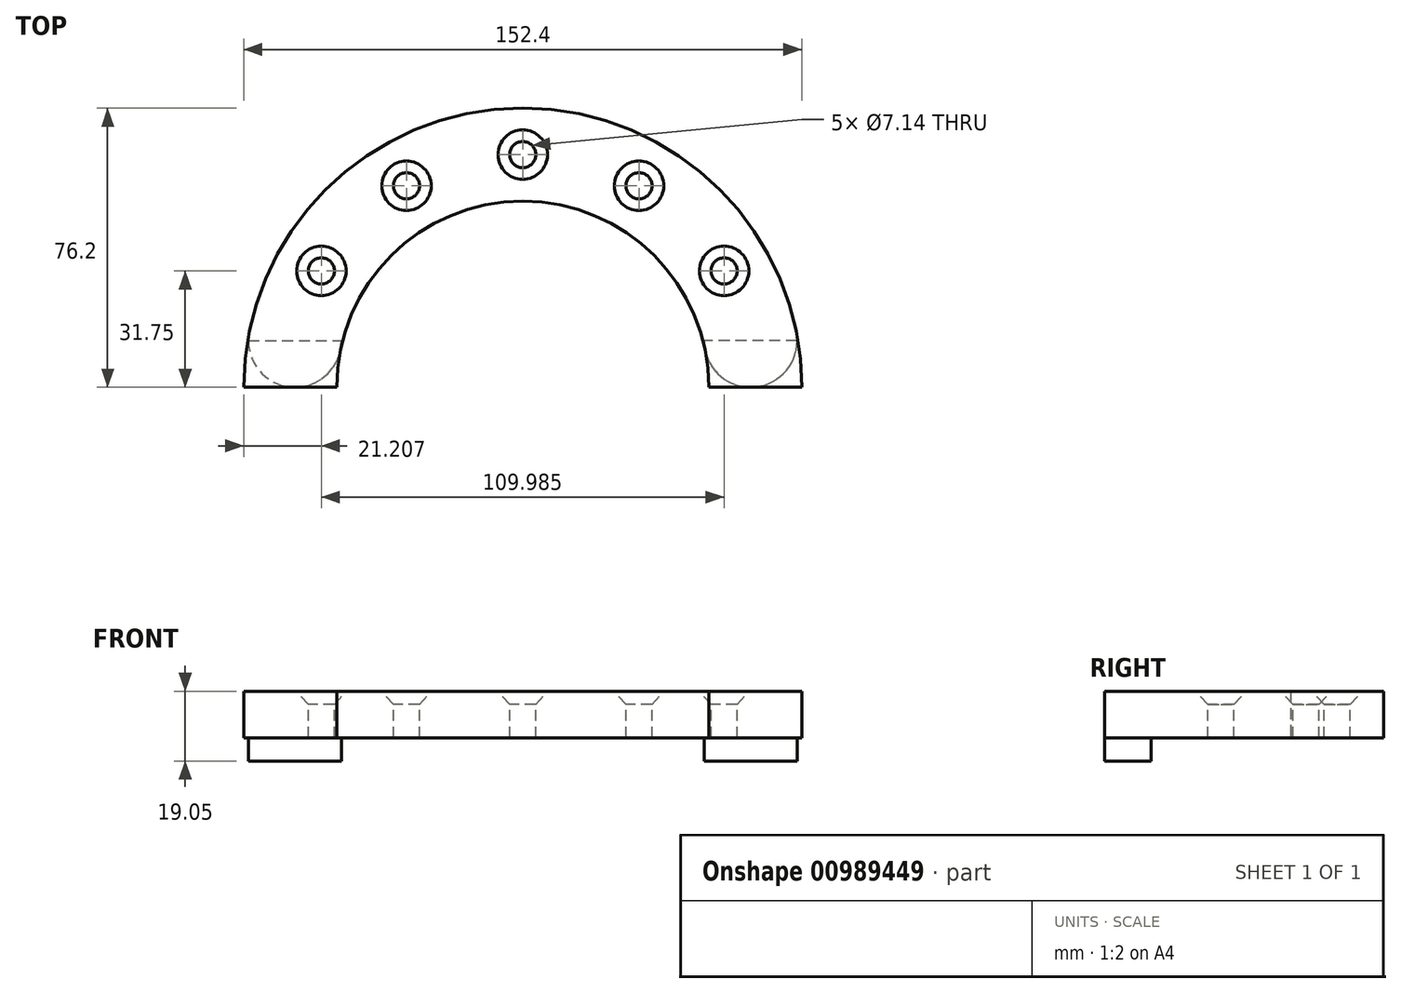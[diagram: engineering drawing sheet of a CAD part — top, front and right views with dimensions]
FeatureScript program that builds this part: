
annotation { "Feature Type Name" : "Feature", "Feature Type Description" : "" }
export const myFeature = defineFeature(function(context is Context, id is Id, definition is map)
    precondition{}
    {
        {
            var Q0;
            Q0=qCreatedBy(makeId("Top.planeOp"),FACE);
            var sketch = newSketch(context, id + "F0", { "sketchPlane" : qUnion([Q0])});
            skArc(sketch, "E0", {"start": v(-50.8, 0) * mm, "mid": v(0, 50.8) * mm, "end": v(50.8, 0) * mm});
            skArc(sketch, "E1", {"start": v(76.2, 0) * mm, "mid": v(0, 76.2) * mm, "end": v(-76.2, 0) * mm});
            skLineSegment(sketch, "E2", {"start": v(-76.2, 0) * mm, "end": v(-50.8, 0) * mm});
            skLineSegment(sketch, "E3", {"start": v(50.8, 0) * mm, "end": v(76.2, 0) * mm});
            skSolve(sketch);
        }
        {
            var Q0;
            Q0 = qSketchRegion(id + "F0", true);
            extrude(context, id + "F1", {"entities" : qUnion([Q0]), "depth" : 12.7 * mm, "offsetDistance" : 25.4 * mm});
        }
        {
            var Q0;
            Q0=makeQuery(id+"F1.opExtrude","CAP_FACE",FACE,{"disambiguationData":[OSD([sQuery(id+"F0.wireOp",EDGE,"E0"),sQuery(id+"F0.wireOp",EDGE,"E1"),sQuery(id+"F0.wireOp",EDGE,"E2"),sQuery(id+"F0.wireOp",EDGE,"E3")])],"isStart":true});
            var sketch = newSketch(context, id + "F2", { "sketchPlane" : qUnion([Q0])});
            skArc(sketch, "E4", {"start": v(-49.52, -12.7) * mm, "mid": v(-62.22, 0) * mm, "end": v(-74.92, -12.7) * mm});
            skLineSegment(sketch, "E5", {"start": v(-74.92, -12.7) * mm, "end": v(-49.52, -12.7) * mm});
            skLineSegment(sketch, "E6", {"start": v(0, 0) * mm, "end": v(0, -90.53) * mm, "construction": true});
            skPoint(sketch, "E6.endSnap0", {"position": v(0, -76.2) * mm});
            skArc(sketch, "E7.MirrorCS", {"start": v(49.52, -12.7) * mm, "mid": v(62.22, 0) * mm, "end": v(74.92, -12.7) * mm});
            skLineSegment(sketch, "E8.MirrorCS", {"start": v(74.92, -12.7) * mm, "end": v(49.52, -12.7) * mm});
            skSolve(sketch);
        }
        {
            var Q0;
            Q0 = qSketchRegion(id + "F2", true);
            extrude(context, id + "F3", {"entities" : qUnion([Q0]), "operationType" : NewBodyOperationType.ADD, "depth" : 6.35 * mm, "offsetDistance" : 25.4 * mm});
        }
        {
            var Q0;
            Q0=makeQuery(id+"F1.opExtrude","CAP_FACE",FACE,{"disambiguationData":[OSD([sQuery(id+"F0.wireOp",EDGE,"E0"),sQuery(id+"F0.wireOp",EDGE,"E1"),sQuery(id+"F0.wireOp",EDGE,"E2"),sQuery(id+"F0.wireOp",EDGE,"E3")])],"isStart":false});
            var sketch = newSketch(context, id + "F4", { "sketchPlane" : qUnion([Q0])});
            skArc(sketch, "E9", {"start": v(-63.5, 0) * mm, "mid": v(0, 63.5) * mm, "end": v(63.5, 0) * mm, "construction": true});
            skPoint(sketch, "E10", {"position": v(-63.5, 0) * mm});
            skPoint(sketch, "E11.1.0", {"position": v(-55, 31.75) * mm});
            skPoint(sketch, "E11.2.0", {"position": v(-31.75, 55) * mm});
            skPoint(sketch, "E11.3.0", {"position": v(0, 63.5) * mm});
            skPoint(sketch, "E11.4.0", {"position": v(31.75, 55) * mm});
            skPoint(sketch, "E11.5.0", {"position": v(55, 31.75) * mm});
            skPoint(sketch, "E11.6.0", {"position": v(63.5, 0) * mm});
            skLineSegment(sketch, "E11.anchor1", {"start": v(0, 0) * mm, "end": v(-63.5, 0) * mm, "construction": true});
            skLineSegment(sketch, "E11.anchor2", {"start": v(0, 0) * mm, "end": v(63.5, 0) * mm, "construction": true});
            skSolve(sketch);
        }
        {
            var Q0;
            Q0=sQuery(id+"F4.wireOp",VERTEX,"E11.1.0");
            var Q1;
            Q1=sQuery(id+"F4.wireOp",VERTEX,"E11.2.0");
            var Q2;
            Q2=sQuery(id+"F4.wireOp",VERTEX,"E11.3.0");
            var Q3;
            Q3=sQuery(id+"F4.wireOp",VERTEX,"E11.4.0");
            var Q4;
            Q4=sQuery(id+"F4.wireOp",VERTEX,"E11.5.0");
            var Q5;
            Q5=makeQuery(id+"F1.opExtrude","SWEPT_BODY",BODY,{"disambiguationData":[OSD([sQuery(id+"F0.wireOp",EDGE,"E0"),sQuery(id+"F0.wireOp",EDGE,"E1"),sQuery(id+"F0.wireOp",EDGE,"E2"),sQuery(id+"F0.wireOp",EDGE,"E3")])]});
            hole(context, id + "F5", {"style" : HoleStyle.C_SINK, "endStyle" : HoleEndStyle.THROUGH, "standardTappedOrClearance" : lookupTablePath({ "fit" : "Normal (ASME)", "standard" : "ANSI", "size" : "1/4", "type" : "Clearance" }), "standardBlindInLast" : lookupTablePath({ "fit" : "Normal", "standard" : "ANSI", "engagement" : "75%", "pitch" : "20 tpi", "size" : "1/4", "type" : "Clearance & tapped" }), "holeDiameter" : 7.14 * mm, "cSinkDiameter" : 13.5 * mm, "cSinkAngle" : 82 * degree, "majorDiameter" : 6.35 * mm, "isTappedThrough" : true, "tappedDepth" : 12.7 * mm, "tapClearance" : 3, "locations" : qUnion([Q0, Q1, Q2, Q3, Q4]), "scope" : qUnion([Q5])});
        }
    });
